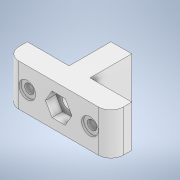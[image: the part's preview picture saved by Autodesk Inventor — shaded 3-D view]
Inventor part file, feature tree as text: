
AUTODESK INVENTOR PART (.ipt)
format: ipt  version: 2020 (Build 240168000, 168)  size: 172,544 bytes
history: native  units: mm
features: extrude x4, sketch x2, other x1, fillet x1
ambient origin geometry x8: Origin, YZ Plane, XZ Plane, XY Plane, X Axis, Y Axis, Z Axis, Center Point
bodies: Body1 (feature_tree)
feature tree (8):
  other  "Bryła1"
  extrude  "Wyciągnięcie proste1"  Depth=20.0mm
  sketch  "Szkic2"
  extrude  "Wyciągnięcie proste2"  Depth=20.0mm
  extrude  "Wyciągnięcie proste3"  Depth=20.0mm
  fillet  "Zaokrąglenie1"  Radius=20.0mm
  extrude  "Wyciągnięcie proste4"  Depth=50.0mm
  sketch  "Szkic1"
